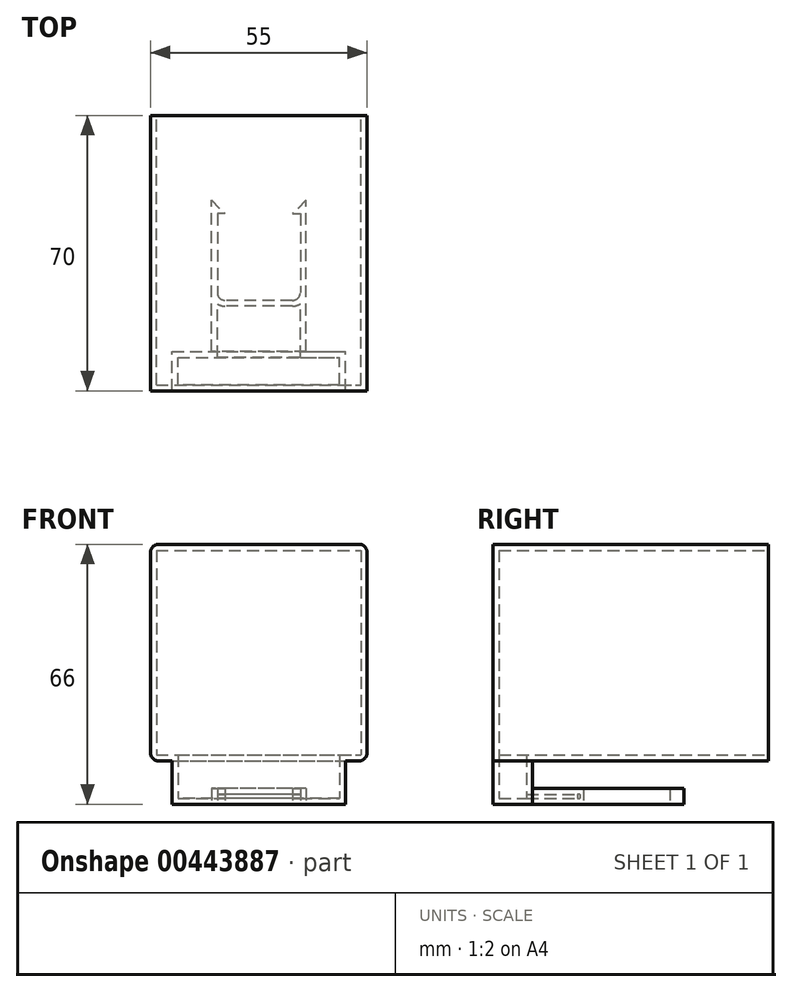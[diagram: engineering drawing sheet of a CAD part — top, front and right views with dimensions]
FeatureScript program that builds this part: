
annotation { "Feature Type Name" : "Feature", "Feature Type Description" : "" }
export const myFeature = defineFeature(function(context is Context, id is Id, definition is map)
    precondition{}
    {
        {
            var Q0;
            Q0=qCreatedBy(makeId("Top.planeOp"),FACE);
            var sketch = newSketch(context, id + "F0", { "sketchPlane" : qUnion([Q0])});
            skLineSegment(sketch, "E0", {"start": v(0, 0) * mm, "end": v(-12.05, 0) * mm});
            skLineSegment(sketch, "E1", {"start": v(-12.05, 0) * mm, "end": v(-12.05, 48.5) * mm});
            skLineSegment(sketch, "E2", {"start": v(-12.05, 48.5) * mm, "end": v(-8.55, 45) * mm});
            skLineSegment(sketch, "E3", {"start": v(-8.55, 45) * mm, "end": v(-10.55, 45) * mm});
            skLineSegment(sketch, "E4", {"start": v(-10.55, 45) * mm, "end": v(-10.55, 23) * mm});
            skLineSegment(sketch, "E5", {"start": v(-10.55, 23) * mm, "end": v(0, 23) * mm});
            skLineSegment(sketch, "E6", {"start": v(0, 23) * mm, "end": v(0, 0) * mm, "construction": true});
            skLineSegment(sketch, "E7.MirrorCS", {"start": v(12.05, 0) * mm, "end": v(12.05, 48.5) * mm});
            skLineSegment(sketch, "E8.MirrorCS", {"start": v(12.05, 48.5) * mm, "end": v(8.55, 45) * mm});
            skLineSegment(sketch, "E9.MirrorCS", {"start": v(8.55, 45) * mm, "end": v(10.55, 45) * mm});
            skLineSegment(sketch, "E10.MirrorCS", {"start": v(10.55, 45) * mm, "end": v(10.55, 23) * mm});
            skLineSegment(sketch, "E11.MirrorCS", {"start": v(10.55, 23) * mm, "end": v(0, 23) * mm});
            skLineSegment(sketch, "E12.MirrorCS", {"start": v(0, 0) * mm, "end": v(12.05, 0) * mm});
            skLineSegment(sketch, "E13.bottom", {"start": v(-22.05, 0) * mm, "end": v(22.05, 0) * mm});
            skLineSegment(sketch, "E13.top", {"start": v(-22.05, 10) * mm, "end": v(22.05, 10) * mm});
            skLineSegment(sketch, "E13.left", {"start": v(-22.05, 0) * mm, "end": v(-22.05, 10) * mm});
            skLineSegment(sketch, "E13.right", {"start": v(22.05, 0) * mm, "end": v(22.05, 10) * mm});
            skSolve(sketch);
        }
        {
            var Q0;
            Q0=makeQuery(id+"F0.imprint","IMPRINT",FACE,{"disambiguationData":[TD([[makeQuery(id+"F0.imprint","IMPRINT",EDGE,{"derivedFrom":sQuery(id+"F0.wireOp",EDGE,"E0")}),-1.0]])]});
            var Q1;
            {var subQ4=sQuery(id+"F0.wireOp",EDGE,"E2");Q1=makeQuery(id+"F0.imprint","IMPRINT",FACE,{"disambiguationData":[TD([[makeQuery(id+"F0.imprint","IMPRINT",EDGE,{"derivedFrom":subQ4}),-1.0]])]});}
            extrude(context, id + "F1", {"entities" : qUnion([Q0, Q1]), "depth" : 4 * mm, "offsetDistance" : 25 * mm});
        }
        {
            var Q0;
            Q0=makeQuery(id+"F1.opExtrude","SWEPT_EDGE",EDGE,{"disambiguationData":[OSD([sQuery(id+"F0.wireOp",EDGE,"E4"),sQuery(id+"F0.wireOp",EDGE,"E5")])]});
            var Q1;
            Q1=makeQuery(id+"F1.opExtrude","SWEPT_EDGE",EDGE,{"disambiguationData":[OSD([sQuery(id+"F0.wireOp",EDGE,"E10.MirrorCS"),sQuery(id+"F0.wireOp",EDGE,"E11.MirrorCS")])]});
            fillet(context, id + "F2", {"entities" : qUnion([Q0, Q1]), "radius" : 2 * mm, "tangentPropagation" : true, "allowEdgeOverflow" : false});
        }
        {
            var Q0;
            {var subQ5=sQuery(id+"F0.wireOp",EDGE,"E13.right");Q0=makeQuery(id+"F0.imprint","IMPRINT",FACE,{"disambiguationData":[TD([[makeQuery(id+"F0.imprint","IMPRINT",EDGE,{"derivedFrom":subQ5}),1.0]])]});}
            var Q1;
            {var subQ0=sQuery(id+"F0.wireOp",EDGE,"E13.bottom");var subQ1=sQuery(id+"F0.wireOp",EDGE,"E1");var subQ2=makeQuery(id+"F0.imprint","INTERSECT",VERTEX,{"derivedFrom":[subQ1,subQ0]});Q1=makeQuery(id+"F0.imprint","IMPRINT",FACE,{"disambiguationData":[TD([[makeQuery(id+"F0.imprint","IMPRINT",EDGE,{"disambiguationData":[TD([[subQ2,-1.0]])],"derivedFrom":subQ1}),-1.0]])]});}
            var Q2;
            {var subQ5=sQuery(id+"F0.wireOp",EDGE,"E13.left");Q2=makeQuery(id+"F0.imprint","IMPRINT",FACE,{"disambiguationData":[TD([[makeQuery(id+"F0.imprint","IMPRINT",EDGE,{"derivedFrom":subQ5}),-1.0]])]});}
            extrude(context, id + "F3", {"entities" : qUnion([Q0, Q1, Q2]), "operationType" : NewBodyOperationType.ADD, "depth" : 11 * mm, "offsetDistance" : 25 * mm});
        }
        {
            var Q0;
            Q0=makeQuery(id+"F3.opExtrude","CAP_FACE",FACE,{"disambiguationData":[OSD([sQuery(id+"F0.wireOp",EDGE,"E13.bottom"),sQuery(id+"F0.wireOp",EDGE,"E13.top"),sQuery(id+"F0.wireOp",EDGE,"E13.left"),sQuery(id+"F0.wireOp",EDGE,"E13.right")])],"isStart":false});
            var sketch = newSketch(context, id + "F4", { "sketchPlane" : qUnion([Q0])});
            skLineSegment(sketch, "E14.bottom", {"start": v(-27.5, 0) * mm, "end": v(27.5, 0) * mm});
            skLineSegment(sketch, "E14.top", {"start": v(-27.5, 70) * mm, "end": v(27.5, 70) * mm});
            skLineSegment(sketch, "E14.left", {"start": v(-27.5, 0) * mm, "end": v(-27.5, 70) * mm});
            skLineSegment(sketch, "E14.right", {"start": v(27.5, 0) * mm, "end": v(27.5, 70) * mm});
            skSolve(sketch);
        }
        {
            var Q0;
            Q0=makeQuery(id+"F4.imprint","IMPRINT",FACE,{"disambiguationData":[TD([[makeQuery(id+"F4.imprint","IMPRINT",EDGE,{"derivedFrom":sQuery(id+"F4.wireOp",EDGE,"E14.top")}),-1.0]])]});
            var Q1;
            Q1=makeQuery(id+"F4.imprint","IMPRINT",FACE,{"disambiguationData":[TD([[makeQuery(id+"F4.imprint","IMPRINT",EDGE,{"derivedFrom":makeQuery(id+"F3.opExtrude","CAP_EDGE",EDGE,{"disambiguationData":[OSD([sQuery(id+"F0.wireOp",EDGE,"E13.top")])],"isStart":false})}),-1.0]])]});
            extrude(context, id + "F5", {"entities" : qUnion([Q0, Q1]), "operationType" : NewBodyOperationType.ADD, "depth" : 55 * mm, "offsetDistance" : 25 * mm});
        }
        {
            var Q0;
            Q0=makeQuery(id+"F5.opExtrude","SWEPT_FACE",FACE,{"disambiguationData":[OSD([sQuery(id+"F4.wireOp",EDGE,"E14.top")])]});
            shell(context, id + "F6", {"entities" : qUnion([Q0]), "thickness" : 1.5 * mm});
        }
        {
            var Q0;
            Q0=makeQuery(id+"F5.opExtrude","CAP_EDGE",EDGE,{"disambiguationData":[OSD([sQuery(id+"F4.wireOp",EDGE,"E14.left")])],"isStart":false});
            var Q1;
            Q1=makeQuery(id+"F5.opExtrude","CAP_EDGE",EDGE,{"disambiguationData":[OSD([sQuery(id+"F4.wireOp",EDGE,"E14.left")])],"isStart":true});
            var Q2;
            Q2=makeQuery(id+"F5.opExtrude","CAP_EDGE",EDGE,{"disambiguationData":[OSD([sQuery(id+"F4.wireOp",EDGE,"E14.right")])],"isStart":true});
            var Q3;
            Q3=makeQuery(id+"F5.opExtrude","CAP_EDGE",EDGE,{"disambiguationData":[OSD([sQuery(id+"F4.wireOp",EDGE,"E14.right")])],"isStart":false});
            fillet(context, id + "F7", {"entities" : qUnion([Q0, Q1, Q2, Q3]), "radius" : 2 * mm, "tangentPropagation" : true, "allowEdgeOverflow" : false});
        }
    });
